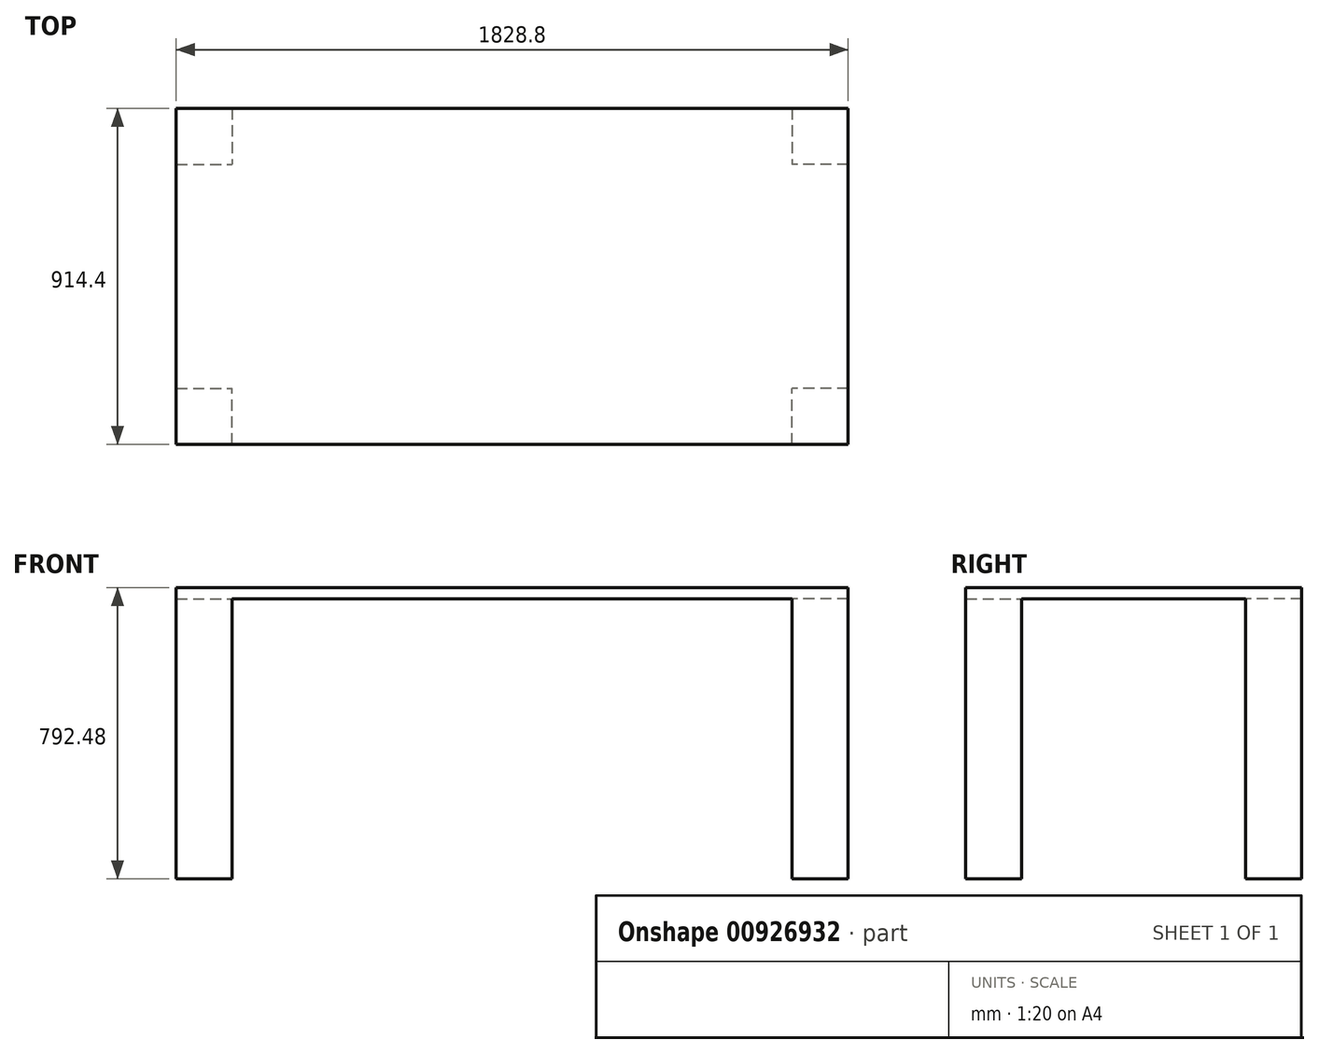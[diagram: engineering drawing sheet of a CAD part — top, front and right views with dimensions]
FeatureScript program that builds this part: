
annotation { "Feature Type Name" : "Feature", "Feature Type Description" : "" }
export const myFeature = defineFeature(function(context is Context, id is Id, definition is map)
    precondition{}
    {
        {
            var Q0;
            Q0=qCreatedBy(makeId("Top.planeOp"),FACE);
            var sketch = newSketch(context, id + "F0", { "sketchPlane" : qUnion([Q0])});
            skLineSegment(sketch, "E0.bottom", {"start": v(914.4, -457.2) * mm, "end": v(-914.4, -457.2) * mm});
            skLineSegment(sketch, "E0.top", {"start": v(914.4, 457.2) * mm, "end": v(-914.4, 457.2) * mm});
            skLineSegment(sketch, "E0.left", {"start": v(914.4, -457.2) * mm, "end": v(914.4, 457.2) * mm});
            skLineSegment(sketch, "E0.right", {"start": v(-914.4, -457.2) * mm, "end": v(-914.4, 457.2) * mm});
            skPoint(sketch, "E0.middle", {"position": v(0, 0) * mm});
            skSolve(sketch);
        }
        {
            var Q0;
            Q0=makeQuery(id+"F0.imprint","IMPRINT",FACE,{"disambiguationData":[TD([[makeQuery(id+"F0.imprint","IMPRINT",EDGE,{"derivedFrom":sQuery(id+"F0.wireOp",EDGE,"E0.bottom")}),-1.0]])]});
            extrude(context, id + "F1", {"entities" : qUnion([Q0]), "depth" : 30.48 * mm, "offsetDistance" : 30.48 * mm});
        }
        {
            var Q0;
            Q0=makeQuery(id+"F1.opExtrude","CAP_FACE",FACE,{"disambiguationData":[OSD([sQuery(id+"F0.wireOp",EDGE,"E0.bottom"),sQuery(id+"F0.wireOp",EDGE,"E0.top"),sQuery(id+"F0.wireOp",EDGE,"E0.left"),sQuery(id+"F0.wireOp",EDGE,"E0.right")])],"isStart":true});
            var sketch = newSketch(context, id + "F2", { "sketchPlane" : qUnion([Q0])});
            skLineSegment(sketch, "E1.bottom", {"start": v(-914.4, 457.2) * mm, "end": v(-762, 457.2) * mm});
            skLineSegment(sketch, "E1.top", {"start": v(-914.4, 304.8) * mm, "end": v(-762, 304.8) * mm});
            skLineSegment(sketch, "E1.left", {"start": v(-914.4, 457.2) * mm, "end": v(-914.4, 304.8) * mm});
            skLineSegment(sketch, "E1.right", {"start": v(-762, 457.2) * mm, "end": v(-762, 304.8) * mm});
            skLineSegment(sketch, "E2.bottom", {"start": v(-914.4, -457.2) * mm, "end": v(-762, -457.2) * mm});
            skLineSegment(sketch, "E2.top", {"start": v(-914.4, -304.8) * mm, "end": v(-762, -304.8) * mm});
            skLineSegment(sketch, "E2.left", {"start": v(-914.4, -457.2) * mm, "end": v(-914.4, -304.8) * mm});
            skLineSegment(sketch, "E2.right", {"start": v(-762, -457.2) * mm, "end": v(-762, -304.8) * mm});
            skLineSegment(sketch, "E3", {"start": v(0, 457.2) * mm, "end": v(0, -457.2) * mm, "construction": true});
            skLineSegment(sketch, "E4.MirrorCS", {"start": v(762, 457.2) * mm, "end": v(762, 304.8) * mm});
            skLineSegment(sketch, "E5.MirrorCS", {"start": v(914.4, 457.2) * mm, "end": v(762, 457.2) * mm});
            skLineSegment(sketch, "E6.MirrorCS", {"start": v(914.4, 457.2) * mm, "end": v(914.4, 304.8) * mm});
            skLineSegment(sketch, "E7.MirrorCS", {"start": v(914.4, 304.8) * mm, "end": v(762, 304.8) * mm});
            skLineSegment(sketch, "E8.MirrorCS", {"start": v(914.4, -304.8) * mm, "end": v(762, -304.8) * mm});
            skLineSegment(sketch, "E9.MirrorCS", {"start": v(914.4, -457.2) * mm, "end": v(914.4, -304.8) * mm});
            skLineSegment(sketch, "E10.MirrorCS", {"start": v(914.4, -457.2) * mm, "end": v(762, -457.2) * mm});
            skLineSegment(sketch, "E11.MirrorCS", {"start": v(762, -457.2) * mm, "end": v(762, -304.8) * mm});
            skSolve(sketch);
        }
        {
            var Q0;
            Q0=makeQuery(id+"F2.imprint","IMPRINT",FACE,{"disambiguationData":[TD([[makeQuery(id+"F2.imprint","IMPRINT",EDGE,{"derivedFrom":sQuery(id+"F2.wireOp",EDGE,"E1.bottom")}),1.0]])]});
            var Q1;
            Q1=makeQuery(id+"F2.imprint","IMPRINT",FACE,{"disambiguationData":[TD([[makeQuery(id+"F2.imprint","IMPRINT",EDGE,{"derivedFrom":sQuery(id+"F2.wireOp",EDGE,"E2.bottom")}),-1.0]])]});
            var Q2;
            Q2=makeQuery(id+"F2.imprint","IMPRINT",FACE,{"disambiguationData":[TD([[makeQuery(id+"F2.imprint","IMPRINT",EDGE,{"derivedFrom":sQuery(id+"F2.wireOp",EDGE,"E8.MirrorCS")}),1.0]])]});
            var Q3;
            Q3=makeQuery(id+"F2.imprint","IMPRINT",FACE,{"disambiguationData":[TD([[makeQuery(id+"F2.imprint","IMPRINT",EDGE,{"derivedFrom":sQuery(id+"F2.wireOp",EDGE,"E4.MirrorCS")}),1.0]])]});
            extrude(context, id + "F3", {"entities" : qUnion([Q0, Q1, Q2, Q3]), "operationType" : NewBodyOperationType.ADD, "depth" : 762 * mm, "offsetDistance" : 30.48 * mm});
        }
    });
